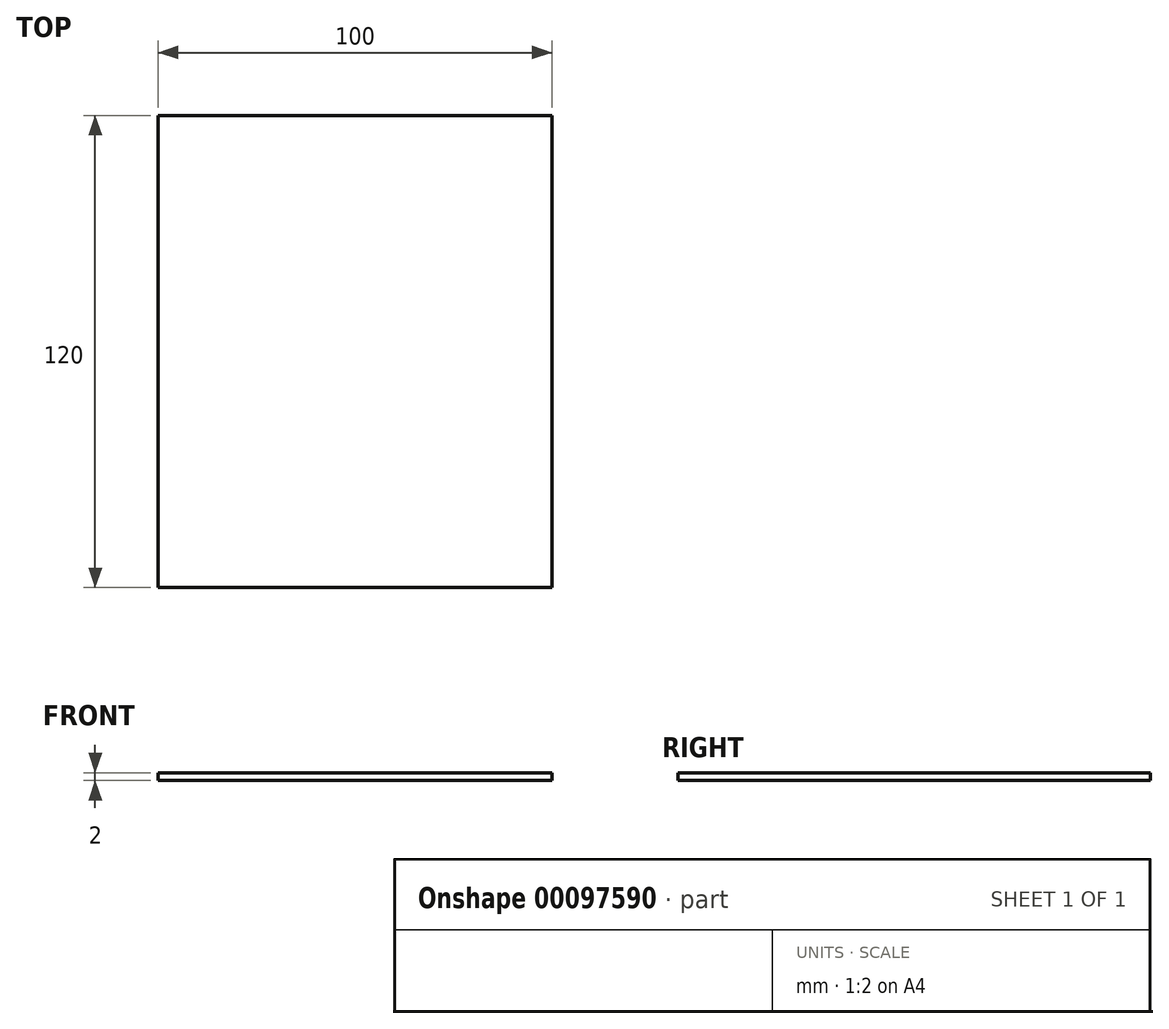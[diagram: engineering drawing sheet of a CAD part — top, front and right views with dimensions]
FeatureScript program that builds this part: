
annotation { "Feature Type Name" : "Feature", "Feature Type Description" : "" }
export const myFeature = defineFeature(function(context is Context, id is Id, definition is map)
    precondition{}
    {
        {
            assignVariable(context, id + "F0", {"name" : "d", "anyValue" : 2});
        }
        {
            var Q0;
            Q0=qCreatedBy(makeId("Top.planeOp"),FACE);
            var sketch = newSketch(context, id + "F1", { "sketchPlane" : qUnion([Q0])});
            skLineSegment(sketch, "E0.bottom", {"start": v(50, 60) * mm, "end": v(-50, 60) * mm});
            skLineSegment(sketch, "E0.top", {"start": v(50, -60) * mm, "end": v(-50, -60) * mm});
            skLineSegment(sketch, "E0.left", {"start": v(50, 60) * mm, "end": v(50, -60) * mm});
            skLineSegment(sketch, "E0.right", {"start": v(-50, 60) * mm, "end": v(-50, -60) * mm});
            skPoint(sketch, "E0.middle", {"position": v(0, 0) * mm});
            skSolve(sketch);
        }
        {
            var Q0;
            Q0=makeQuery(id+"F1.imprint","IMPRINT",FACE,{"disambiguationData":[TD([[makeQuery(id+"F1.imprint","IMPRINT",EDGE,{"derivedFrom":sQuery(id+"F1.wireOp",EDGE,"E0.bottom")}),1.0]])]});
            extrude(context, id + "F2", {"entities" : qUnion([Q0]), "depth" : (getVariable(context, 'd')) * mm});
        }
    });
